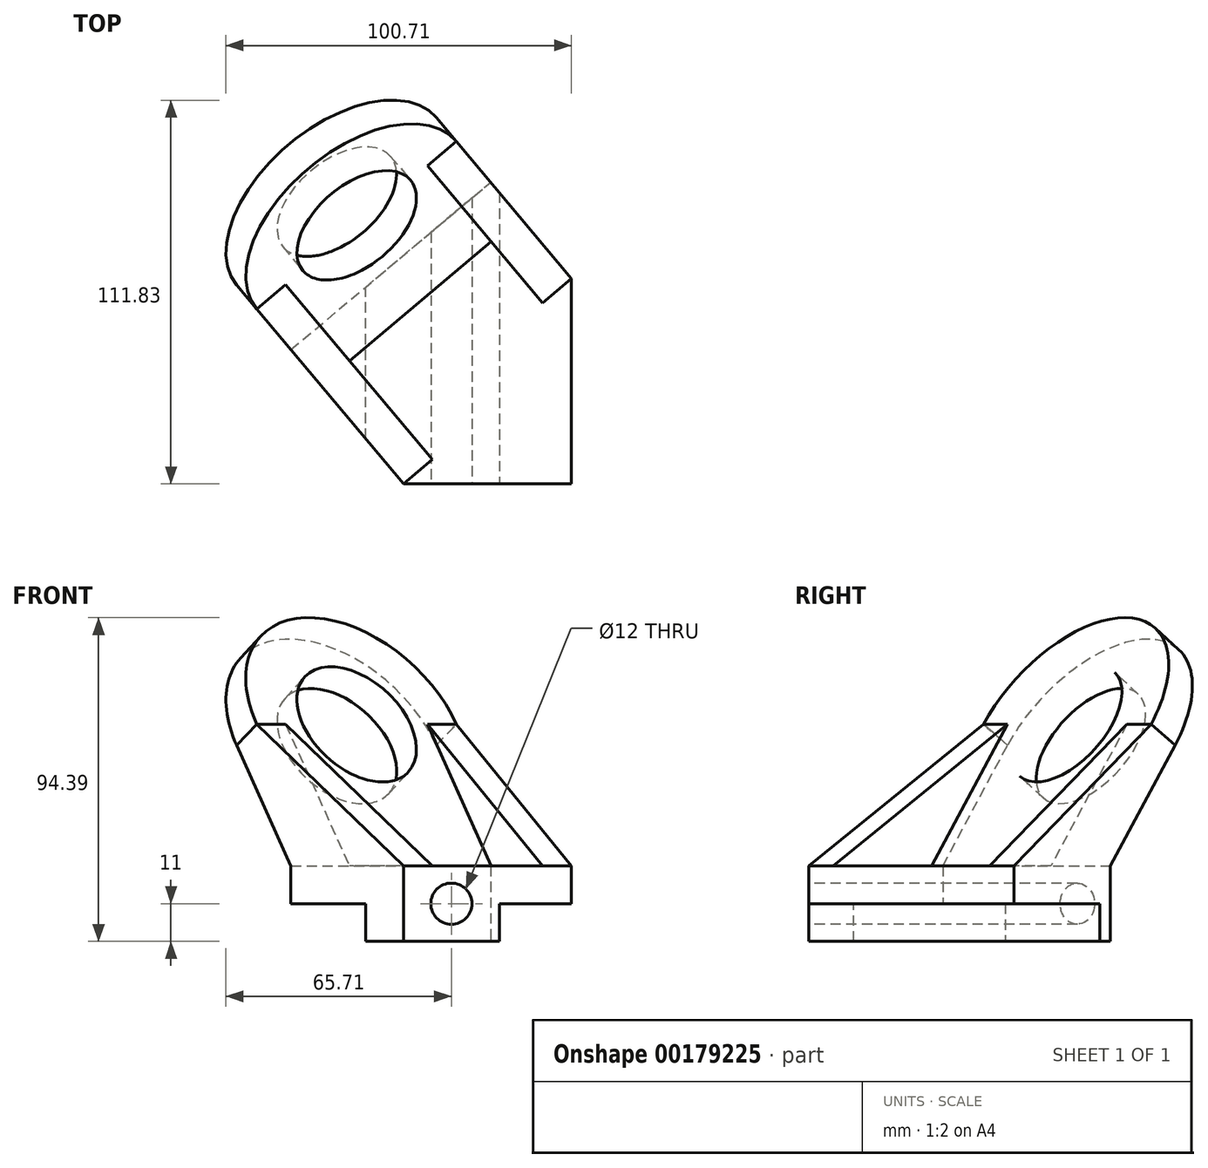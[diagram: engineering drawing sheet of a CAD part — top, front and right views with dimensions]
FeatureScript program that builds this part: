
annotation { "Feature Type Name" : "Feature", "Feature Type Description" : "" }
export const myFeature = defineFeature(function(context is Context, id is Id, definition is map)
    precondition{}
    {
        {
            var Q0;
            Q0=qCreatedBy(makeId("Top.planeOp"),FACE);
            var sketch = newSketch(context, id + "F0", { "sketchPlane" : qUnion([Q0])});
            skLineSegment(sketch, "E0", {"start": v(0, 0) * mm, "end": v(-49, 0) * mm});
            skLineSegment(sketch, "E1", {"start": v(-49, 0) * mm, "end": v(-81.78, 39.07) * mm});
            skLineSegment(sketch, "E2", {"start": v(-81.78, 39.07) * mm, "end": v(-23.56, 87.92) * mm});
            skLineSegment(sketch, "E3", {"start": v(-23.56, 87.92) * mm, "end": v(0, 59.84) * mm});
            skLineSegment(sketch, "E4", {"start": v(0, 0) * mm, "end": v(0, 59.84) * mm});
            skSolve(sketch);
        }
        {
            var Q0;
            Q0 = qSketchRegion(id + "F0", true);
            extrude(context, id + "F1", {"entities" : qUnion([Q0]), "depth" : 22 * mm});
        }
        {
            var Q0;
            Q0=makeQuery(id+"F1.opExtrude","SWEPT_FACE",FACE,{"disambiguationData":[OSD([sQuery(id+"F0.wireOp",EDGE,"E0")])]});
            var sketch = newSketch(context, id + "F2", { "sketchPlane" : qUnion([Q0])});
            skLineSegment(sketch, "E5.bottom", {"start": v(0, 0) * mm, "end": v(-21, 0) * mm});
            skLineSegment(sketch, "E5.top", {"start": v(0, 11) * mm, "end": v(-21, 11) * mm});
            skLineSegment(sketch, "E5.left", {"start": v(0, 0) * mm, "end": v(0, 11) * mm});
            skLineSegment(sketch, "E5.right", {"start": v(-21, 0) * mm, "end": v(-21, 11) * mm});
            skLineSegment(sketch, "E6.bottom", {"start": v(-60, -1.48) * mm, "end": v(-100.01, -1.48) * mm});
            skLineSegment(sketch, "E6.top", {"start": v(-60, 11) * mm, "end": v(-100.01, 11) * mm});
            skLineSegment(sketch, "E6.left", {"start": v(-60, -1.48) * mm, "end": v(-60, 11) * mm});
            skLineSegment(sketch, "E6.right", {"start": v(-100.01, -1.48) * mm, "end": v(-100.01, 11) * mm});
            skSolve(sketch);
        }
        {
            var Q0;
            Q0 = qSketchRegion(id + "F2", true);
            extrude(context, id + "F3", {"entities" : qUnion([Q0]), "operationType" : NewBodyOperationType.REMOVE, "endBound" : BoundingType.THROUGH_ALL, "oppositeDirection" : true, "depth" : 25 * mm});
        }
        {
            var Q0;
            Q0=makeQuery(id+"F1.opExtrude","SWEPT_FACE",FACE,{"disambiguationData":[OSD([sQuery(id+"F0.wireOp",EDGE,"E0")])]});
            var sketch = newSketch(context, id + "F4", { "sketchPlane" : qUnion([Q0])});
            skCircle(sketch, "E7", {"center": v(-35, 11) * mm, "radius": 6 * mm});
            skSolve(sketch);
        }
        {
            var Q0;
            Q0=makeQuery(id+"F4.imprint","IMPRINT",FACE,{"disambiguationData":[TD([[makeQuery(id+"F4.imprint","IMPRINT",EDGE,{"derivedFrom":sQuery(id+"F4.wireOp",EDGE,"E7")}),1.0]])]});
            extrude(context, id + "F5", {"entities" : qUnion([Q0]), "operationType" : NewBodyOperationType.REMOVE, "endBound" : BoundingType.THROUGH_ALL, "oppositeDirection" : true, "depth" : 25 * mm});
        }
        {
            var Q0;
            Q0=makeQuery(id+"F1.opExtrude","SWEPT_FACE",FACE,{"disambiguationData":[OSD([sQuery(id+"F0.wireOp",EDGE,"E1")])]});
            var sketch = newSketch(context, id + "F6", { "sketchPlane" : qUnion([Q0])});
            skLineSegment(sketch, "E8", {"start": v(-82.5, 22) * mm, "end": v(-107.16, 57.22) * mm});
            skLineSegment(sketch, "E9", {"start": v(-107.16, 57.22) * mm, "end": v(-97.97, 63.27) * mm});
            skLineSegment(sketch, "E10", {"start": v(-97.97, 63.27) * mm, "end": v(-69.07, 22) * mm});
            skLineSegment(sketch, "E11", {"start": v(-82.5, 22) * mm, "end": v(-69.07, 22) * mm});
            skPoint(sketch, "E12.orphan", {"position": v(-57, 22) * mm});
            skSolve(sketch);
        }
        {
            var Q0;
            Q0 = qSketchRegion(id + "F6", true);
            var Q1;
            Q1=makeQuery(id+"F1.opExtrude","SWEPT_FACE",FACE,{"disambiguationData":[OSD([sQuery(id+"F0.wireOp",EDGE,"E3")])]});
            extrude(context, id + "F7", {"entities" : qUnion([Q0]), "operationType" : NewBodyOperationType.ADD, "endBound" : BoundingType.UP_TO_SURFACE, "oppositeDirection" : true, "endBoundEntityFace" : qUnion([Q1]), "depth" : 25 * mm});
        }
        {
            var Q0;
            Q0=makeQuery(id+"F7.opExtrude","SWEPT_FACE",FACE,{"disambiguationData":[OSD([sQuery(id+"F6.wireOp",EDGE,"E10")])]});
            var sketch = newSketch(context, id + "F8", { "sketchPlane" : qUnion([Q0])});
            skArc(sketch, "E13", {"start": v(-12.19, 114.01) * mm, "mid": v(-62.9, 131.77) * mm, "end": v(-80.67, 81.05) * mm});
            skLineSegment(sketch, "E14", {"start": v(-80.67, 81.05) * mm, "end": v(-12.19, 114.01) * mm});
            skSolve(sketch);
        }
        {
            var Q0;
            Q0 = qSketchRegion(id + "F8", true);
            var Q1;
            Q1=makeQuery(id+"F7.opExtrude","SWEPT_FACE",FACE,{"disambiguationData":[OSD([sQuery(id+"F6.wireOp",EDGE,"E8")])]});
            extrude(context, id + "F9", {"entities" : qUnion([Q0]), "operationType" : NewBodyOperationType.ADD, "endBound" : BoundingType.UP_TO_SURFACE, "oppositeDirection" : true, "endBoundEntityFace" : qUnion([Q1]), "depth" : 25 * mm});
        }
        {
            var Q0;
            Q0=makeQuery(id+"F9.boolean.opBoolean","MERGE",FACE,{"derivedFrom":[makeQuery(id+"F7.opExtrude","SWEPT_FACE",FACE,{"disambiguationData":[OSD([sQuery(id+"F6.wireOp",EDGE,"E10")])]}),makeQuery(id+"F9.opExtrude","CAP_FACE",FACE,{"disambiguationData":[OSD([sQuery(id+"F8.wireOp",EDGE,"E13"),sQuery(id+"F8.wireOp",EDGE,"E14")])],"isStart":true})]});
            var sketch = newSketch(context, id + "F10", { "sketchPlane" : qUnion([Q0])});
            skCircle(sketch, "E15", {"center": v(-46.43, 97.53) * mm, "radius": 20.5 * mm});
            skSolve(sketch);
        }
        {
            var Q0;
            Q0 = qSketchRegion(id + "F10", true);
            extrude(context, id + "F11", {"entities" : qUnion([Q0]), "operationType" : NewBodyOperationType.REMOVE, "endBound" : BoundingType.THROUGH_ALL, "oppositeDirection" : true, "depth" : 25 * mm});
        }
        {
            var Q0;
            Q0=makeQuery(id+"F7.boolean.opBoolean","MERGE",FACE,{"derivedFrom":[makeQuery(id+"F1.opExtrude","SWEPT_FACE",FACE,{"disambiguationData":[OSD([sQuery(id+"F0.wireOp",EDGE,"E1")])]}),makeQuery(id+"F7.opExtrude","CAP_FACE",FACE,{"disambiguationData":[OSD([sQuery(id+"F6.wireOp",EDGE,"E8"),sQuery(id+"F6.wireOp",EDGE,"E9"),sQuery(id+"F6.wireOp",EDGE,"E10"),sQuery(id+"F6.wireOp",EDGE,"E11")])],"isStart":true})]});
            var sketch = newSketch(context, id + "F12", { "sketchPlane" : qUnion([Q0])});
            skLineSegment(sketch, "E16", {"start": v(-97.97, 63.27) * mm, "end": v(-31.5, 22) * mm});
            skLineSegment(sketch, "E17", {"start": v(-31.5, 22) * mm, "end": v(-69.07, 22) * mm});
            skLineSegment(sketch, "E18", {"start": v(-69.07, 22) * mm, "end": v(-97.97, 63.27) * mm});
            skSolve(sketch);
        }
        {
            var Q0;
            Q0 = qSketchRegion(id + "F12", true);
            extrude(context, id + "F13", {"entities" : qUnion([Q0]), "operationType" : NewBodyOperationType.ADD, "oppositeDirection" : true, "depth" : 11 * mm});
        }
        {
            var Q0;
            {var subQ0=sQuery(id+"F0.wireOp",EDGE,"E3");Q0=makeQuery(id+"F7.boolean.opBoolean","MERGE",FACE,{"derivedFrom":[makeQuery(id+"F1.opExtrude","SWEPT_FACE",FACE,{"disambiguationData":[OSD([subQ0])]}),makeQuery(id+"F7.opExtrude","CAP_FACE",FACE,{"disambiguationData":[OSD([subQ0])],"isStart":false})]});}
            var sketch = newSketch(context, id + "F14", { "sketchPlane" : qUnion([Q0])});
            skLineSegment(sketch, "E19.0", {"start": v(97.97, 63.27) * mm, "end": v(69.07, 22) * mm});
            skLineSegment(sketch, "E20.0", {"start": v(69.07, 22) * mm, "end": v(45.84, 22) * mm});
            skLineSegment(sketch, "E21", {"start": v(45.84, 22) * mm, "end": v(97.97, 63.27) * mm});
            skSolve(sketch);
        }
        {
            var Q0;
            Q0 = qSketchRegion(id + "F14", true);
            extrude(context, id + "F15", {"entities" : qUnion([Q0]), "operationType" : NewBodyOperationType.ADD, "oppositeDirection" : true, "depth" : 11 * mm});
        }
    });
